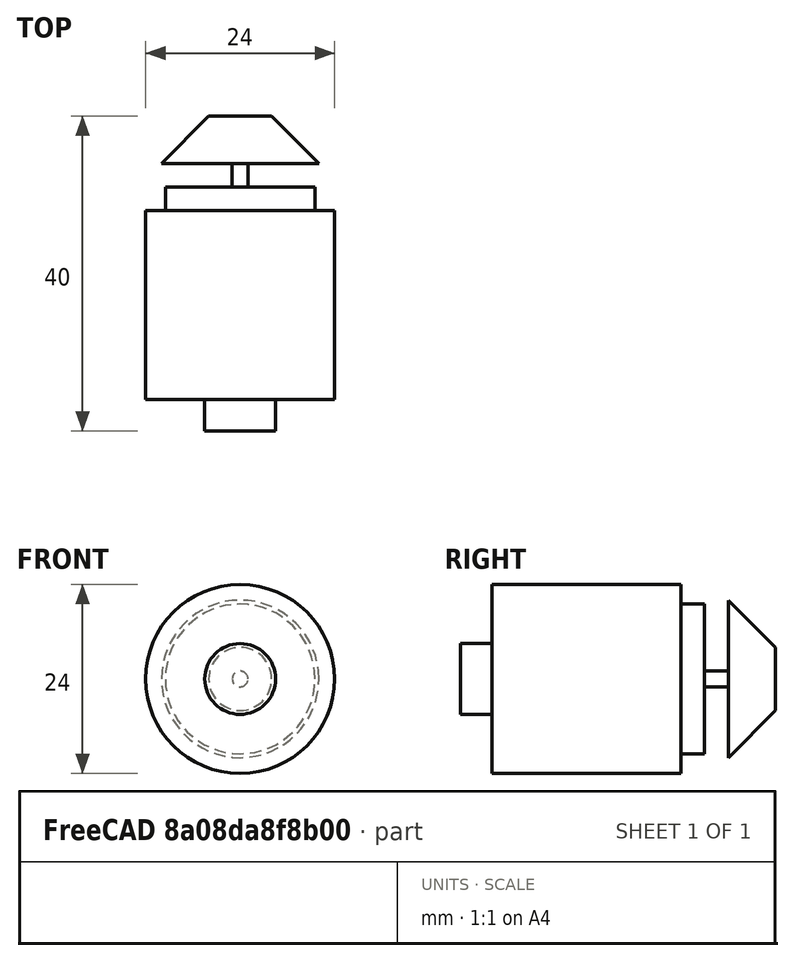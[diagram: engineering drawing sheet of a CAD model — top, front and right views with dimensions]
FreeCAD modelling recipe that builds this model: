
FCSTD DOCUMENT  (FreeCAD 0.14R3700 (Git))
Label: BR_Moteur
License: CC-BY 3.0
LicenseURL: http://creativecommons.org/licenses/by/3.0/
objects: Sketcher::SketchObject×1, Part::Revolution×1, Part::Feature×1
note: 3 computed .brp shape members not serialized (recipe doc carries the construction recipe); baked Part::Feature solids carry a one-line shape summary decoded from their .brp

FEATURE [Sketcher::SketchObject] Sketch  label="moteur"
  Placement = pos=(0,0,0) rot=(0.57735,0.57735,0.57735;2.0944rad)
  sketch-geometry (12):
    g0: LineSegment StartX=0 StartY=0 StartZ=0 EndX=0 EndY=4.5 EndZ=0
    g1: LineSegment StartX=0 StartY=4.5 StartZ=0 EndX=4 EndY=4.5 EndZ=0
    g2: LineSegment StartX=4 StartY=4.5 StartZ=0 EndX=4 EndY=12 EndZ=0
    g3: LineSegment StartX=4 StartY=12 StartZ=0 EndX=28 EndY=12 EndZ=0
    g4: LineSegment StartX=28 StartY=12 StartZ=0 EndX=28 EndY=9.5 EndZ=0
    g5: LineSegment StartX=28 StartY=9.5 StartZ=0 EndX=31 EndY=9.5 EndZ=0
    g6: LineSegment StartX=31 StartY=9.5 StartZ=0 EndX=31 EndY=1 EndZ=0
    g7: LineSegment StartX=31 StartY=1 StartZ=0 EndX=34 EndY=1 EndZ=0
    g8: LineSegment StartX=34 StartY=1 StartZ=0 EndX=34 EndY=10 EndZ=0
    g9: LineSegment StartX=34 StartY=10 StartZ=0 EndX=40 EndY=4 EndZ=0
    g10: LineSegment StartX=40 StartY=4 StartZ=0 EndX=40 EndY=0 EndZ=0
    g11: LineSegment StartX=40 StartY=0 StartZ=0 EndX=0 EndY=0 EndZ=0
  constraints (35):
    c: Coincident(g0,g-1)
    c: Vertical(g0)
    c: Coincident(g1,g0)
    c: Horizontal(g1)
    c: Coincident(g2,g1)
    c: Vertical(g2)
    c: Coincident(g3,g2)
    c: Horizontal(g3)
    c: Coincident(g4,g3)
    c: Vertical(g4)
    c: Coincident(g5,g4)
    c: Horizontal(g5)
    c: Coincident(g6,g5)
    c: Vertical(g6)
    c: Coincident(g7,g6)
    c: Horizontal(g7)
    c: Coincident(g8,g7)
    c: Vertical(g8)
    c: Coincident(g9,g8)
    c: Coincident(g10,g9)
    c: Vertical(g10)
    c: Coincident(g11,g10)
    c: Horizontal(g11)
    c: Coincident(g11,g-1)
    c: DistanceY(g-1,g6) = 1
    c: DistanceY(g-1,g8) = 10
    c: Angle(g8,g9) = 0.785398
    c: DistanceX(g8,g9) = 6
    c: DistanceY(g0) = 4.5
    c: DistanceX(g1) = 4
    c: DistanceY(g-1,g2) = 12
    c: DistanceX(g3) = 24
    c: DistanceX(g2,g5) = 27
    c: DistanceY(g-1,g5) = 9.5
    c: DistanceX(g7) = 3
FEATURE [Part::Revolution] Revolve
  Angle = 360
  Axis = (0,1,0)
  Base = (0,0,0)
  Solid = false
  Source = -> Sketch
FEATURE [Part::Feature] Revolve001  label="moteur_copy"
  shape: bbox 24 x 40 x 24 mm, 11 faces, 0 solids (baked)
